# Revit family: Gira_291503
name_source: partatom
category: Electrical Fixtures
revit_build: Autodesk Revit 2017 (Build: 20160225_1515(x64)
units: mm (PartAtom-declared; Revit-internal decimal feet)

## family parameters
Cut with Voids When Loaded = No
Host = Face
Maintain Annotation Orientation = Yes
Part Type = Normal
Room Calculation Point = No
Round Connector Dimension = Use Diameter
Shared = No

## types (1)
- Duty room unit emergency set System 55 p.white
    Assembly arrangement = Basic element
    Available = No
    BIM (1) = https://media.stage.bim.site und Tasten.rfa?public/gira/36a6b08/Sys55_Komplettgerät_Schalten und Tasten.rfa
    Button function = Quit call
    Category = Call-/control unit clinic-installation
    Colour = White
    Construction = Wall model
    Data sheet (1) = https://katalog.gira.de
    Default Elevation = 1219 mm
    Description = Duty room u.emerg.set Sys55 PW,Duty room unit for the emergency set,System 55,pure white glossy,Features:,- Duty room unit (without display) with call acknowledgement (green keypad) and switch-off button for the buzzer (yellow keypad).,,Notes :,- The duty room unit is an optional component of the emergency set.
    GTIN = 4010337069720
    HAN = 291503
    HeinzeBIM = https://bimportal.heinze.de
    Manufacturer = Gira
    Manufacturer URL = https://www.gira.de
    Material = Other
    Material quality = Other
    Name = Duty room unit emergency set System 55 p.white
    Operation = Button
    Suitable for = Call
    Suitable for bus connection = 2-wire
    Type of power supply = Bus system
    URL = http://katalog.gira.de

## geometry (parser evidence)
native form markers: Blend x2, Sweep x9
no freeform markers — native parametric forms only
